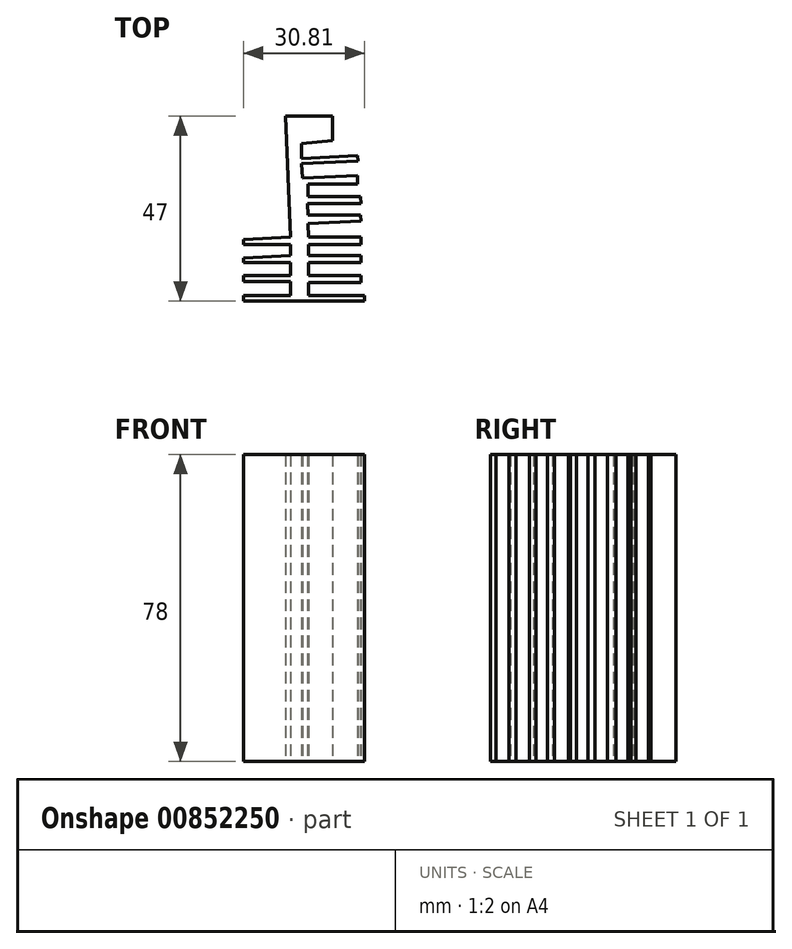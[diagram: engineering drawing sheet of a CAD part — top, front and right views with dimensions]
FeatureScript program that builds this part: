
annotation { "Feature Type Name" : "Feature", "Feature Type Description" : "" }
export const myFeature = defineFeature(function(context is Context, id is Id, definition is map)
    precondition{}
    {
        {
            var Q0;
            Q0=qCreatedBy(makeId("Top.planeOp"),FACE);
            var sketch = newSketch(context, id + "F0", { "sketchPlane" : qUnion([Q0])});
            skLineSegment(sketch, "E0", {"start": v(-10.1, 26.27) * mm, "end": v(-8.75, -4.54) * mm});
            skLineSegment(sketch, "E1", {"start": v(-8.75, -4.54) * mm, "end": v(-20.75, -5.06) * mm});
            skLineSegment(sketch, "E2", {"start": v(-20.75, -5.06) * mm, "end": v(-20.75, -6.36) * mm});
            skLineSegment(sketch, "E3", {"start": v(-20.75, -6.36) * mm, "end": v(-8.75, -6.36) * mm});
            skLineSegment(sketch, "E4", {"start": v(-8.75, -6.36) * mm, "end": v(-8.75, -9.2) * mm});
            skLineSegment(sketch, "E5", {"start": v(-8.75, -9.2) * mm, "end": v(-20.75, -9.84) * mm});
            skLineSegment(sketch, "E6", {"start": v(-20.75, -9.84) * mm, "end": v(-20.75, -10.94) * mm});
            skLineSegment(sketch, "E7", {"start": v(-20.75, -10.94) * mm, "end": v(-8.75, -10.94) * mm});
            skLineSegment(sketch, "E8", {"start": v(-8.75, -10.94) * mm, "end": v(-8.75, -14.26) * mm});
            skLineSegment(sketch, "E9", {"start": v(-8.75, -14.26) * mm, "end": v(-20.75, -14.26) * mm});
            skLineSegment(sketch, "E10", {"start": v(-20.75, -14.26) * mm, "end": v(-20.75, -15.76) * mm});
            skLineSegment(sketch, "E11", {"start": v(-20.75, -15.76) * mm, "end": v(-8.75, -15.76) * mm});
            skLineSegment(sketch, "E12", {"start": v(-8.75, -15.76) * mm, "end": v(-8.75, -19.4) * mm});
            skLineSegment(sketch, "E13", {"start": v(-8.75, -19.4) * mm, "end": v(-20.75, -19.4) * mm});
            skLineSegment(sketch, "E14", {"start": v(-20.75, -19.4) * mm, "end": v(-20.75, -20.73) * mm});
            skLineSegment(sketch, "E15", {"start": v(10.06, -20.73) * mm, "end": v(10.06, -19.4) * mm});
            skLineSegment(sketch, "E16", {"start": v(10.06, -19.4) * mm, "end": v(-4.25, -19.4) * mm});
            skLineSegment(sketch, "E17", {"start": v(-4.25, -19.4) * mm, "end": v(-4.25, -16.04) * mm});
            skLineSegment(sketch, "E18", {"start": v(-4.25, -16.04) * mm, "end": v(9.1, -16.04) * mm});
            skLineSegment(sketch, "E19", {"start": v(9.1, -16.04) * mm, "end": v(9.1, -14.26) * mm});
            skLineSegment(sketch, "E20", {"start": v(9.1, -14.26) * mm, "end": v(-4.25, -14.26) * mm});
            skLineSegment(sketch, "E21", {"start": v(-4.25, -14.26) * mm, "end": v(-4.25, -10.94) * mm});
            skLineSegment(sketch, "E22", {"start": v(-4.25, -10.94) * mm, "end": v(9.1, -10.94) * mm});
            skLineSegment(sketch, "E23", {"start": v(9.1, -10.94) * mm, "end": v(9.1, -9.2) * mm});
            skLineSegment(sketch, "E24", {"start": v(9.1, -9.2) * mm, "end": v(-4.25, -9.2) * mm});
            skLineSegment(sketch, "E25", {"start": v(-4.25, -9.2) * mm, "end": v(-4.25, -6.36) * mm});
            skLineSegment(sketch, "E26", {"start": v(-4.25, -6.36) * mm, "end": v(9.1, -6.36) * mm});
            skLineSegment(sketch, "E27", {"start": v(9.1, -6.36) * mm, "end": v(9.1, -4.54) * mm});
            skLineSegment(sketch, "E28", {"start": v(9.1, -4.54) * mm, "end": v(-4.25, -4.54) * mm});
            skLineSegment(sketch, "E29", {"start": v(-4.25, -4.54) * mm, "end": v(-4.4, -1) * mm});
            skLineSegment(sketch, "E30", {"start": v(-4.4, -1) * mm, "end": v(9.1, -0.42) * mm});
            skLineSegment(sketch, "E31", {"start": v(9.1, -0.42) * mm, "end": v(9.04, 1.1) * mm});
            skLineSegment(sketch, "E32", {"start": v(9.04, 1.1) * mm, "end": v(-4.4, 1.1) * mm});
            skLineSegment(sketch, "E33", {"start": v(-4.4, 1.1) * mm, "end": v(-4.53, 4) * mm});
            skLineSegment(sketch, "E34", {"start": v(-4.53, 4) * mm, "end": v(9.1, 4) * mm});
            skLineSegment(sketch, "E35", {"start": v(9.1, 4) * mm, "end": v(9.03, 5.76) * mm});
            skLineSegment(sketch, "E36", {"start": v(9.03, 5.76) * mm, "end": v(-4.4, 5.76) * mm});
            skLineSegment(sketch, "E37", {"start": v(-4.4, 5.76) * mm, "end": v(-4.4, 8.93) * mm});
            skLineSegment(sketch, "E38", {"start": v(-4.4, 8.93) * mm, "end": v(8.24, 8.93) * mm});
            skLineSegment(sketch, "E39", {"start": v(8.24, 8.93) * mm, "end": v(8.24, 11.14) * mm});
            skLineSegment(sketch, "E40", {"start": v(-10.1, 26.27) * mm, "end": v(1.93, 26.27) * mm});
            skLineSegment(sketch, "E41", {"start": v(1.93, 26.27) * mm, "end": v(1.93, 20) * mm});
            skLineSegment(sketch, "E42", {"start": v(1.93, 20) * mm, "end": v(-5.95, 19.29) * mm});
            skLineSegment(sketch, "E43", {"start": v(-5.95, 19.29) * mm, "end": v(-5.95, 15.47) * mm});
            skLineSegment(sketch, "E44", {"start": v(-5.95, 15.47) * mm, "end": v(8.24, 16.17) * mm});
            skLineSegment(sketch, "E45", {"start": v(8.24, 16.17) * mm, "end": v(8.3, 14.87) * mm});
            skLineSegment(sketch, "E46", {"start": v(8.3, 14.87) * mm, "end": v(-5.95, 14.16) * mm});
            skLineSegment(sketch, "E47", {"start": v(-5.95, 14.16) * mm, "end": v(-5.77, 10.52) * mm});
            skLineSegment(sketch, "E48", {"start": v(-5.77, 10.52) * mm, "end": v(8.24, 11.14) * mm});
            skLineSegment(sketch, "E49", {"start": v(10.06, -20.73) * mm, "end": v(-20.75, -20.73) * mm});
            skSolve(sketch);
        }
        {
            var Q0;
            Q0=makeQuery(id+"F0.imprint","IMPRINT",FACE,{"disambiguationData":[TD([[makeQuery(id+"F0.imprint","IMPRINT",EDGE,{"derivedFrom":sQuery(id+"F0.wireOp",EDGE,"E0")}),1.0]])]});
            extrude(context, id + "F1", {"entities" : qUnion([Q0]), "depth" : 78 * mm, "offsetDistance" : 25 * mm});
        }
    });
